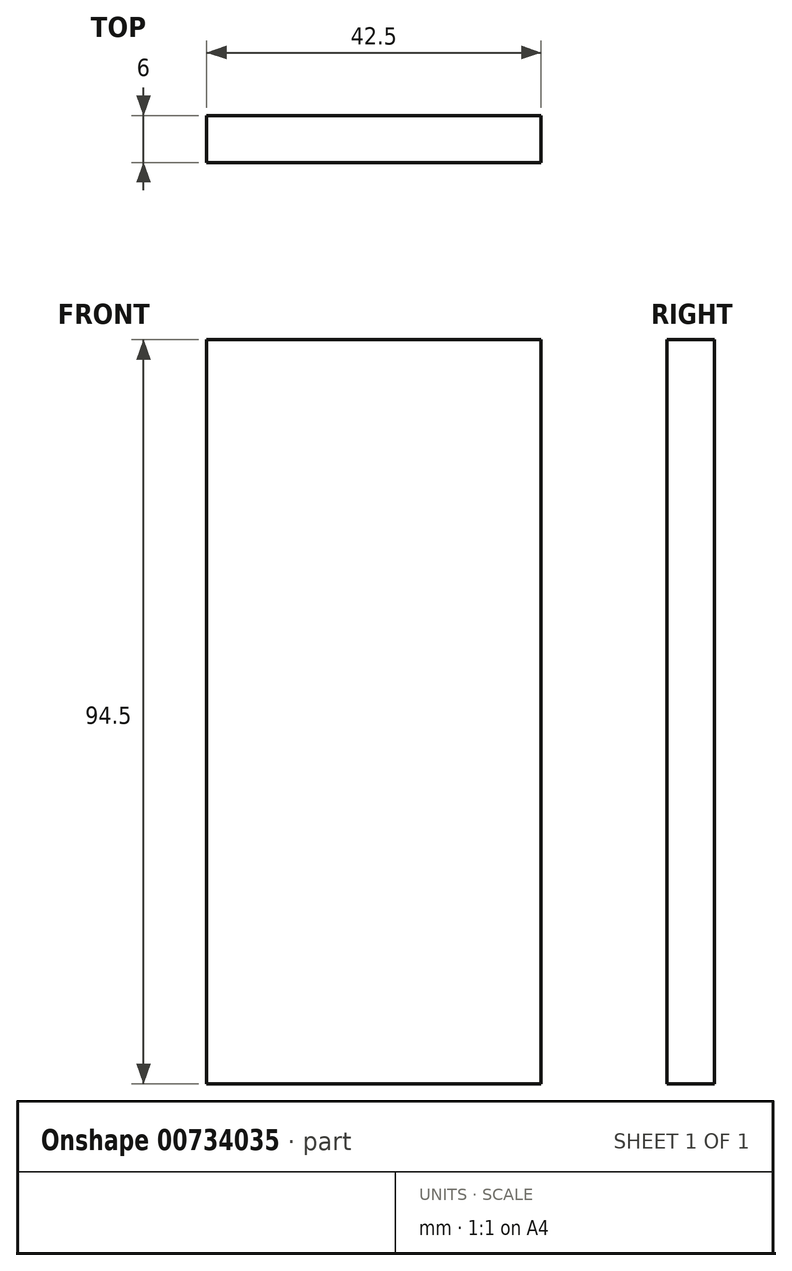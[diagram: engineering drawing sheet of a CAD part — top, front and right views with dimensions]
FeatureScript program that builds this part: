
annotation { "Feature Type Name" : "Feature", "Feature Type Description" : "" }
export const myFeature = defineFeature(function(context is Context, id is Id, definition is map)
    precondition{}
    {
        {
            var Q0;
            Q0=qCreatedBy(makeId("Front.planeOp"),FACE);
            var sketch = newSketch(context, id + "F0", { "sketchPlane" : qUnion([Q0])});
            skLineSegment(sketch, "E0.bottom", {"start": v(-22.95, 45.06) * mm, "end": v(19.55, 45.06) * mm});
            skLineSegment(sketch, "E0.top", {"start": v(-22.95, -49.44) * mm, "end": v(19.55, -49.44) * mm});
            skLineSegment(sketch, "E0.left", {"start": v(-22.95, 45.06) * mm, "end": v(-22.95, -49.44) * mm});
            skLineSegment(sketch, "E0.right", {"start": v(19.55, 45.06) * mm, "end": v(19.55, -49.44) * mm});
            skSolve(sketch);
        }
        {
            var Q0;
            Q0=qSketchRegion(id+"F0",true);
            extrude(context, id + "F1", {"entities" : qUnion([Q0]), "depth" : 6 * mm, "offsetDistance" : 25 * mm});
        }
    });
